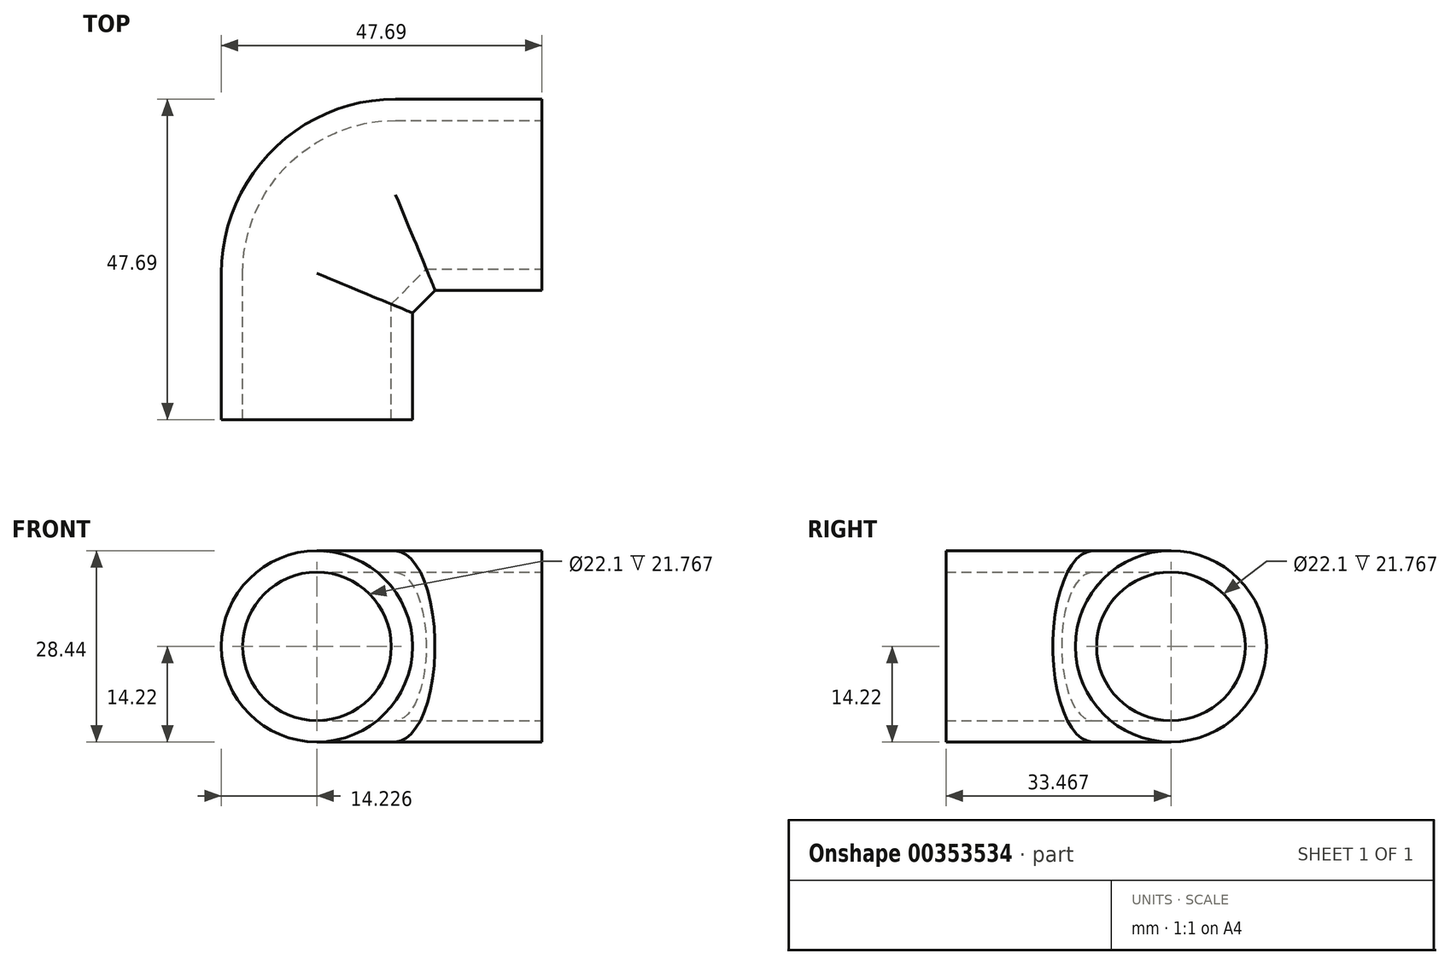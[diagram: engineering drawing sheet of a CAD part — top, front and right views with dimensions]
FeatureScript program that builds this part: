
annotation { "Feature Type Name" : "Feature", "Feature Type Description" : "" }
export const myFeature = defineFeature(function(context is Context, id is Id, definition is map)
    precondition{}
    {
        {
            var Q0;
            Q0=qCreatedBy(makeId("Top.planeOp"),FACE);
            var sketch = newSketch(context, id + "F0", { "sketchPlane" : qUnion([Q0])});
            skLineSegment(sketch, "E0", {"start": v(0, 0) * mm, "end": v(0, 15.88) * mm});
            skLineSegment(sketch, "E1", {"start": v(3.37, 19.24) * mm, "end": v(19.24, 19.24) * mm});
            skLineSegment(sketch, "E2", {"start": v(19.24, 19.24) * mm, "end": v(0, 0) * mm, "construction": true});
            skLineSegment(sketch, "E3", {"start": v(0, 15.88) * mm, "end": v(3.37, 19.24) * mm});
            skSolve(sketch);
        }
        {
            var Q0;
            Q0=qCreatedBy(makeId("Front.planeOp"),FACE);
            var sketch = newSketch(context, id + "F1", { "sketchPlane" : qUnion([Q0])});
            skArc(sketch, "E4", {"start": v(-14.22, -14.22) * mm, "mid": v(0, 0) * mm, "end": v(-14.22, 14.22) * mm});
            skLineSegment(sketch, "E5", {"start": v(-14.22, 0) * mm, "end": v(-14.22, 14.22) * mm});
            skLineSegment(sketch, "E6", {"start": v(-14.22, 0) * mm, "end": v(-14.22, -14.22) * mm});
            skSolve(sketch);
        }
        {
            var Q0;
            Q0 = qSketchRegion(id + "F1", true);
            var Q1;
            Q1 = qConstructionFilter(qBodyType(qCreatedBy(id + "F0" ,EDGE), BodyType.WIRE), ConstructionObject.NO);
            sweep(context, id + "F2", {"profiles" : qUnion([Q0]), "path" : qUnion([Q1])});
        }
        {
            var Q0;
            Q0=qCreatedBy(makeId("Top.planeOp"),FACE);
            var sketch = newSketch(context, id + "F3", { "sketchPlane" : qUnion([Q0])});
            skLineSegment(sketch, "E7.0", {"start": v(-14.22, 0) * mm, "end": v(-14.22, 21.77) * mm});
            skSolve(sketch);
        }
        {
            var Q0;
            Q0=makeQuery(id+"F2.opSweep","CAP_FACE",FACE,{"disambiguationData":[OSD([sQuery(id+"F0.wireOp",VERTEX,"E0.start"),sQuery(id+"F1.wireOp",EDGE,"E4"),sQuery(id+"F1.wireOp",EDGE,"E5"),sQuery(id+"F1.wireOp",EDGE,"E6")])],"isStart":true});
            var sketch = newSketch(context, id + "F4", { "sketchPlane" : qUnion([Q0])});
            skArc(sketch, "E8", {"start": v(-14.22, 14.22) * mm, "mid": v(-28.45, 0) * mm, "end": v(-14.22, -14.22) * mm});
            skLineSegment(sketch, "E9", {"start": v(-14.22, 14.22) * mm, "end": v(-14.22, -14.22) * mm});
            skSolve(sketch);
        }
        {
            var Q0;
            Q0 = qSketchRegion(id + "F4", true);
            var Q1;
            Q1 = qConstructionFilter(qBodyType(qCreatedBy(id + "F3" ,EDGE), BodyType.WIRE), ConstructionObject.NO);
            sweep(context, id + "F5", {"operationType" : NewBodyOperationType.ADD, "profiles" : qUnion([Q0]), "path" : qUnion([Q1])});
        }
        {
            var Q0;
            Q0=qCreatedBy(makeId("Top.planeOp"),FACE);
            var sketch = newSketch(context, id + "F6", { "sketchPlane" : qUnion([Q0])});
            skLineSegment(sketch, "E10.0", {"start": v(-2.52, 33.47) * mm, "end": v(19.24, 33.47) * mm});
            skSolve(sketch);
        }
        {
            var Q0;
            Q0=makeQuery(id+"F2.opSweep","CAP_FACE",FACE,{"disambiguationData":[OSD([sQuery(id+"F0.wireOp",VERTEX,"E1.end"),sQuery(id+"F1.wireOp",EDGE,"E4"),sQuery(id+"F1.wireOp",EDGE,"E5"),sQuery(id+"F1.wireOp",EDGE,"E6")])],"isStart":false});
            var sketch = newSketch(context, id + "F7", { "sketchPlane" : qUnion([Q0])});
            skArc(sketch, "E11", {"start": v(33.47, -14.22) * mm, "mid": v(47.7, 0) * mm, "end": v(33.47, 14.22) * mm});
            skLineSegment(sketch, "E12", {"start": v(33.47, 14.22) * mm, "end": v(33.47, -14.22) * mm});
            skSolve(sketch);
        }
        {
            var Q0;
            Q0 = qSketchRegion(id + "F7", true);
            var Q1;
            Q1 = qConstructionFilter(qBodyType(qCreatedBy(id + "F6" ,EDGE), BodyType.WIRE), ConstructionObject.NO);
            sweep(context, id + "F8", {"operationType" : NewBodyOperationType.ADD, "profiles" : qUnion([Q0]), "path" : qUnion([Q1])});
        }
        {
            var Q0;
            Q0=qCreatedBy(makeId("Top.planeOp"),FACE);
            var sketch = newSketch(context, id + "F9", { "sketchPlane" : qUnion([Q0])});
            skPoint(sketch, "E13.0", {"position": v(-2.52, 33.47) * mm});
            skPoint(sketch, "E14.0", {"position": v(-14.22, 21.77) * mm});
            skLineSegment(sketch, "E15.bottom", {"start": v(-2.52, 33.47) * mm, "end": v(-14.22, 33.47) * mm, "construction": true});
            skLineSegment(sketch, "E15.top", {"start": v(-2.52, 21.77) * mm, "end": v(-14.22, 21.77) * mm, "construction": true});
            skLineSegment(sketch, "E15.left", {"start": v(-2.52, 33.47) * mm, "end": v(-2.52, 21.77) * mm, "construction": true});
            skLineSegment(sketch, "E15.right", {"start": v(-14.22, 33.47) * mm, "end": v(-14.22, 21.77) * mm, "construction": true});
            skArc(sketch, "E16", {"start": v(-2.52, 33.47) * mm, "mid": v(-10.8, 30.04) * mm, "end": v(-14.22, 21.77) * mm});
            skSolve(sketch);
        }
        {
            var Q0;
            Q0=makeQuery(id+"F5.opSweep","CAP_FACE",FACE,{"disambiguationData":[OSD([sQuery(id+"F3.wireOp",VERTEX,"E7.0.end"),sQuery(id+"F4.wireOp",EDGE,"E8"),sQuery(id+"F4.wireOp",EDGE,"E9")])],"isStart":false});
            var sketch = newSketch(context, id + "F10", { "sketchPlane" : qUnion([Q0])});
            skArc(sketch, "E17.0.1", {"start": v(14.22, -14.22) * mm, "mid": v(28.45, 0) * mm, "end": v(14.22, 14.22) * mm});
            skArc(sketch, "E18.0", {"start": v(14.22, 14.22) * mm, "mid": v(10.08, 13.6) * mm, "end": v(6.3, 11.8) * mm});
            skLineSegment(sketch, "E19", {"start": v(14.22, 0) * mm, "end": v(6.3, 11.8) * mm});
            skLineSegment(sketch, "E20", {"start": v(14.22, 0) * mm, "end": v(6.3, -11.8) * mm});
            skArc(sketch, "E21.trimOffspring", {"start": v(6.3, -11.8) * mm, "mid": v(10.08, -13.6) * mm, "end": v(14.22, -14.22) * mm});
            skSolve(sketch);
        }
        {
            var Q0;
            Q0 = qSketchRegion(id + "F10", true);
            var Q1;
            Q1 = qConstructionFilter(qBodyType(qCreatedBy(id + "F9" ,EDGE), BodyType.WIRE), ConstructionObject.NO);
            sweep(context, id + "F11", {"operationType" : NewBodyOperationType.ADD, "profiles" : qUnion([Q0]), "path" : qUnion([Q1])});
        }
        {
            var Q0;
            Q0=makeQuery(id+"F2.opSweep","SWEPT_EDGE",EDGE,{"disambiguationData":[OSD([sQuery(id+"F0.wireOp",EDGE,"E3"),sQuery(id+"F1.wireOp",EDGE,"E4"),sQuery(id+"F1.wireOp",EDGE,"E5")])]});
            cPlane(context, id + "F12", {"entities" : qUnion([Q0]), "cplaneType" : CPlaneType.MID_PLANE, "offset" : 25.4 * mm, "width" : 152.4 * mm, "height" : 152.4 * mm});
        }
        {
            var Q0;
            Q0=qCreatedBy(id+"F12.planeOp",FACE);
            var sketch = newSketch(context, id + "F13", { "sketchPlane" : qUnion([Q0])});
            skPoint(sketch, "E22.0", {"position": v(25.45, 14.22) * mm});
            skLineSegment(sketch, "E23", {"start": v(25.45, 14.22) * mm, "end": v(50.33, 14.22) * mm, "construction": true});
            skSolve(sketch);
        }
        {
            var Q0;
            Q0=sQuery(id+"F13.wireOp",VERTEX,"E23.end");
            var Q1;
            Q1=sQuery(id+"F13.wireOp",VERTEX,"E22.0");
            var Q2;
            {var subQ0=sQuery(id+"F7.wireOp",EDGE,"E12");var subQ1=sQuery(id+"F7.wireOp",EDGE,"E11");var subQ2=sQuery(id+"F1.wireOp",EDGE,"E4");var subQ3=sQuery(id+"F0.wireOp",VERTEX,"E1.end");var subQ4=sQuery(id+"F6.wireOp",EDGE,"E10.0");Q2=makeQuery(id+"F8.boolean.opBoolean","MERGE",VERTEX,{"derivedFrom":[makeQuery(id+"F2.opSweep","MID_CAP_VERTEX",VERTEX,{"disambiguationData":[OSD([sQuery(id+"F0.wireOp",EDGE,"E3"),subQ2,sQuery(id+"F1.wireOp",EDGE,"E5")])],"capPos":2.0}),makeQuery(id+"F8.opSweep","CAP_VERTEX",VERTEX,{"disambiguationData":[OSD([subQ3,subQ2,subQ4,subQ1,subQ0]),TDD([subQ4,makeQuery(id+"F7.imprint","INTERSECT",VERTEX,{"disambiguationData":[OD(1.0)],"derivedFrom":[makeQuery(id+"F2.opSweep","CAP_EDGE",EDGE,{"disambiguationData":[OSD([subQ3,subQ2])],"isStart":false}),subQ1,subQ0]})])],"isStart":false})]});}
            cPlane(context, id + "F14", {"entities" : qUnion([Q0, Q1, Q2]), "cplaneType" : CPlaneType.THREE_POINT, "offset" : 25.4 * mm, "width" : 152.4 * mm, "height" : 152.4 * mm});
        }
        {
            var Q0;
            Q0=qCreatedBy(id+"F14.planeOp",FACE);
            var sketch = newSketch(context, id + "F15", { "sketchPlane" : qUnion([Q0])});
            skPoint(sketch, "E24.0", {"position": v(-14.22, -21.77) * mm});
            skPoint(sketch, "E25.0", {"position": v(-2.52, -33.47) * mm});
            skLineSegment(sketch, "E26", {"start": v(-2.52, -33.47) * mm, "end": v(-14.22, -21.77) * mm});
            skLineSegment(sketch, "E27", {"start": v(-10.8, -30.04) * mm, "end": v(-8.37, -27.62) * mm});
            skArc(sketch, "E28", {"start": v(-14.22, -21.77) * mm, "mid": v(-10.8, -30.04) * mm, "end": v(-2.52, -33.47) * mm});
            skSolve(sketch);
        }
        {
            var Q0;
            Q0 = qSketchRegion(id + "F15", true);
            extrude(context, id + "F16", {"entities" : qUnion([Q0]), "operationType" : NewBodyOperationType.ADD, "depth" : 28.45 * mm});
        }
        {
            var Q0;
            Q0=makeQuery(id+"F5.boolean.opBoolean","MERGE",FACE,{"derivedFrom":[makeQuery(id+"F2.opSweep","CAP_FACE",FACE,{"disambiguationData":[OSD([sQuery(id+"F0.wireOp",VERTEX,"E0.start"),sQuery(id+"F1.wireOp",EDGE,"E4"),sQuery(id+"F1.wireOp",EDGE,"E5"),sQuery(id+"F1.wireOp",EDGE,"E6")])],"isStart":true}),makeQuery(id+"F5.opSweep","CAP_FACE",FACE,{"disambiguationData":[OSD([sQuery(id+"F3.wireOp",VERTEX,"E7.0.start"),sQuery(id+"F4.wireOp",EDGE,"E8"),sQuery(id+"F4.wireOp",EDGE,"E9")])],"isStart":true})]});
            var Q1;
            Q1=makeQuery(id+"F8.boolean.opBoolean","MERGE",FACE,{"derivedFrom":[makeQuery(id+"F2.opSweep","CAP_FACE",FACE,{"disambiguationData":[OSD([sQuery(id+"F0.wireOp",VERTEX,"E1.end"),sQuery(id+"F1.wireOp",EDGE,"E4"),sQuery(id+"F1.wireOp",EDGE,"E5"),sQuery(id+"F1.wireOp",EDGE,"E6")])],"isStart":false}),makeQuery(id+"F8.opSweep","CAP_FACE",FACE,{"disambiguationData":[OSD([sQuery(id+"F6.wireOp",VERTEX,"E10.0.end"),sQuery(id+"F7.wireOp",EDGE,"E11"),sQuery(id+"F7.wireOp",EDGE,"E12")])],"isStart":true})]});
            shell(context, id + "F17", {"entities" : qUnion([Q0, Q1]), "thickness" : 3.17 * mm});
        }
    });
